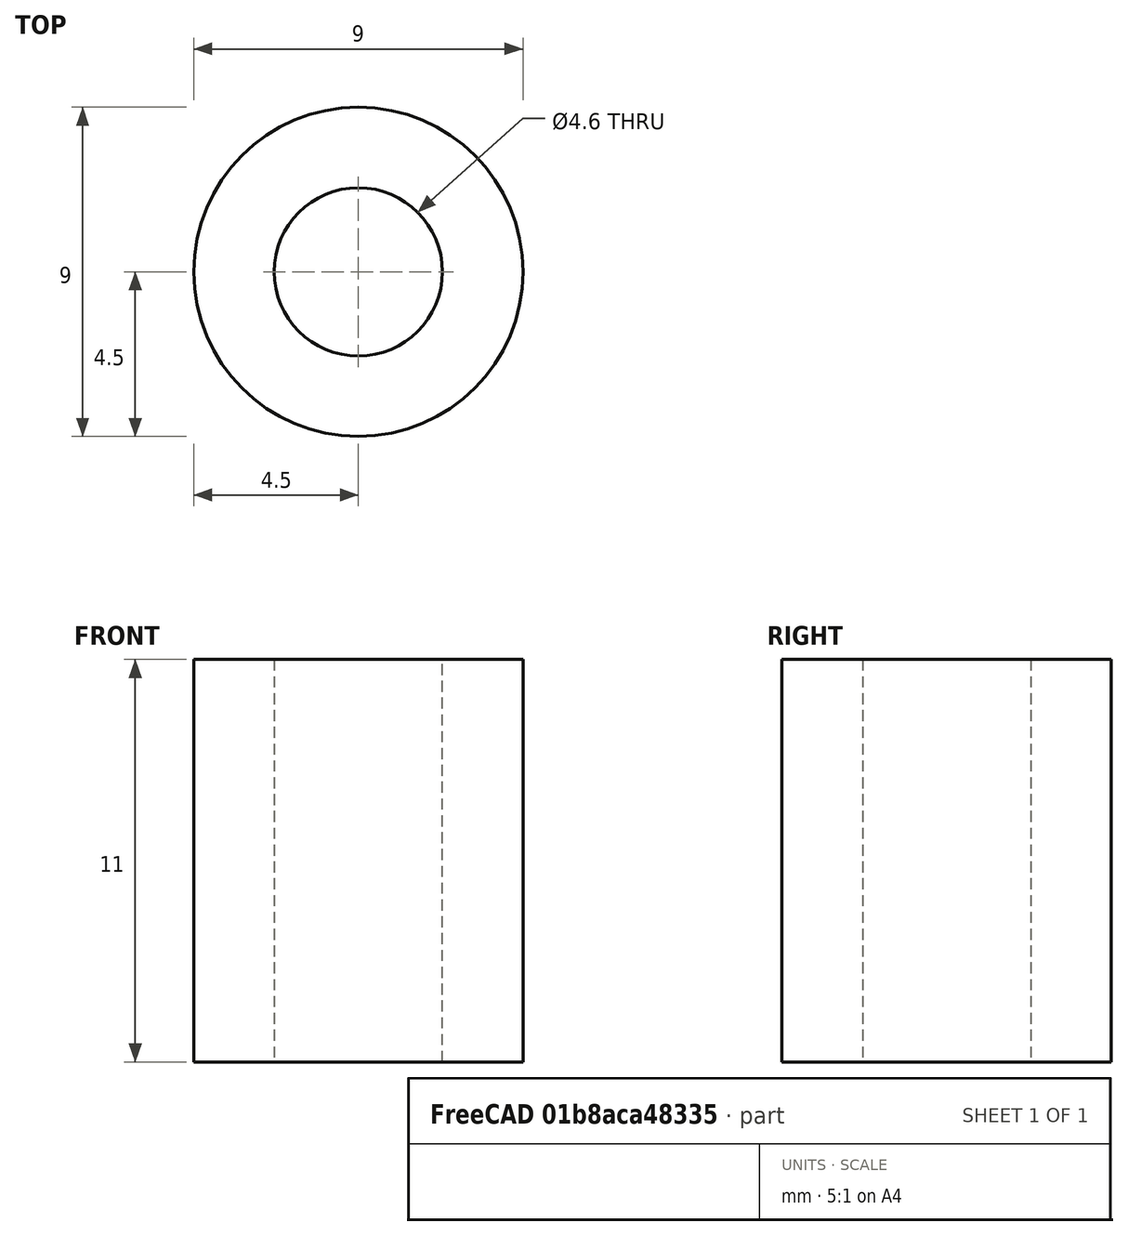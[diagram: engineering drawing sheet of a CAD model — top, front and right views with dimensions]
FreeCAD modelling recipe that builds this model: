
FCSTD DOCUMENT  (FreeCAD 0.20R25065 (Git))
Label: cf-spacer
License: All rights reserved
LicenseURL: http://en.wikipedia.org/wiki/All_rights_reserved
objects: Sketcher::SketchObject×1, PartDesign::Pad×1, PartDesign::Body×1
note: 4 computed .brp shape members not serialized (recipe doc carries the construction recipe); baked Part::Feature solids carry a one-line shape summary decoded from their .brp

FEATURE [Sketcher::SketchObject] Sketch
  FullyConstrained = true
  MapMode = 5
  Support = -> [XY_Plane]
  sketch-geometry (2):
    g0: Circle CenterX=0 CenterY=0 CenterZ=0 NormalX=0 NormalY=0 NormalZ=1 AngleXU=0 Radius=4.5
    g1: Circle CenterX=0 CenterY=0 CenterZ=0 NormalX=0 NormalY=0 NormalZ=1 AngleXU=0 Radius=2.3
  constraints (4):
    c: Coincident(g0,g-1)
    c: Coincident(g1,g0)
    c: Radius(g1) = 2.3
    c: Radius(g0) = 4.5
FEATURE [PartDesign::Pad] Pad
  Direction = (0,0,1)
  Length = 11
  Length2 = 100
  Profile = -> Sketch
  Refine = true
  Type = 0
FEATURE [PartDesign::Body] Body
  Group = -> [Sketch,Pad]
  Origin = -> Origin
  Tip = -> Pad
